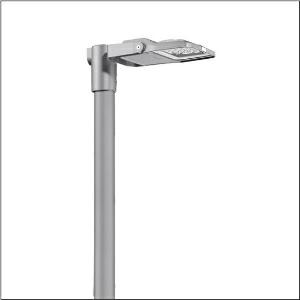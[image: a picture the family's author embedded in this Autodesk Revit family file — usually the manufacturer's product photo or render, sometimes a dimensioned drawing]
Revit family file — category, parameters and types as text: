
# Revit family: floodlight_fl_21_iq_micro___pl61_5xa7761a4c3a_000e
name_source: partatom
category: Lighting Fixtures
units: mm (PartAtom-declared; Revit-internal decimal feet)

## family parameters
Cut with Voids When Loaded = No
Host = Face
Light Source = No
Part Type = Normal
Room Calculation Point = No
Round Connector Dimension = Use Diameter
Shared = No

## types (1)
- --- (1 x LED, 3030 lm, 23.1 W, 4000K)
    Apparent Load = 23 VA
    CIE Flux Codes = 33 65 98 100 100
    Color Rendering = 70
    Color Temperature = 4000K
    Default Elevation = 1800 mm
    Description = Floodlight FL 21 iQ micro, floodlight, primary light control with lens, of PMMA, primary optical cover: protective disc, of toughened safety glass, transparent, light distribution: PL61, light emission: direct distribution, installation type: surface-mounted, LED, High Power LED, rated luminous flux: 3.030lm, luminous efficacy: 131lm/W, light colour: 740, colour temperature: 4000K, control: optimised constant luminous flux control (CLO 2.0), Desk-Remote (wireless, voltage-free reading and setting of iQ features in the workshop via application-optimized NFC function/RFID function), Light-Fading, Smart-Wire, Night-Set, Lumen-Switch, Temp-Guard, Auto-Match, with terminal, 6-pole, mains connection: 220..240V, AC, 50/60Hz, start of lifetime: 23W, end of service life: 24W, reduction: 11W, luminaire housing, of diecast aluminium, powder-coated, Siteco® metallic grey (DB 702S), corrosivity category C5 mid according to DIN EN ISO 12944, sealing non-destructively replaceable, please order mast flange separately, mast bracket, of steel, galvanised, powder-coated, Siteco® metallic grey (DB 702S), protection rating (complete): IP66, insulation class (complete): insulation class II (safety insulation), certification: CE, ENEC, VDE, protection symbol: D, impact resistance: IK07, permissible operating ambient temperature: -40..+40°C, permissible operating ambient temperature for outdoor applications: -40..+50°C, standard: DIN EN 12944, LABS conformity tested according to VDMA 24364:2018-05, packaging unit: 1 piece

Light Distribution: PL61
    Height = 65 mm
    Lamp = 1 x LED
    Lamp Light Flux = 3030 lm
    Lamp Power = 23.1 W
    Lamp count = 1
    Length = 312 mm
    Luminous efficacy = 131 lm/W
    Manufacturer = Siteco
    ModVariant = No
    Model = 5XA7761A4C3A
    Number of Poles = 1
    OnlyDefault = Yes
    Power Factor = 1
    Product Name = Floodlight FL 21 iQ micro | PL61
    Product group = floodlight | pylon annexe
    ProductGroupID = 6200
    Protection Class = Protection class II
    Protection Degree = IP 66
    RLX_Detail_Level = 1
    RLX_Emergency_Light_Flux = 0 lm
    RLX_Emergency_Type = 0
    RLX_Emergency_Type_DB = No
    RlxData = <blob elided: 101893 chars, md5=12f8c2dd>
    Socket = socket
    Standby Power = 0 W
    System Light Flux = 3030 lm
    System Power = 23 W
    Type Comments = factory setting: luminous flux: 100 % | dim-lin: 254 | 455 mA
    Type Image = l_1007121.jpg
    URL = http://relux.com
    VarID = @adj_147157
    Voltage = 0 V
    Weight = 0.00 kg
    Width = 230 mm

## geometry (parser evidence)
native form markers: Blend x4, Sweep x12
no freeform markers — native parametric forms only
